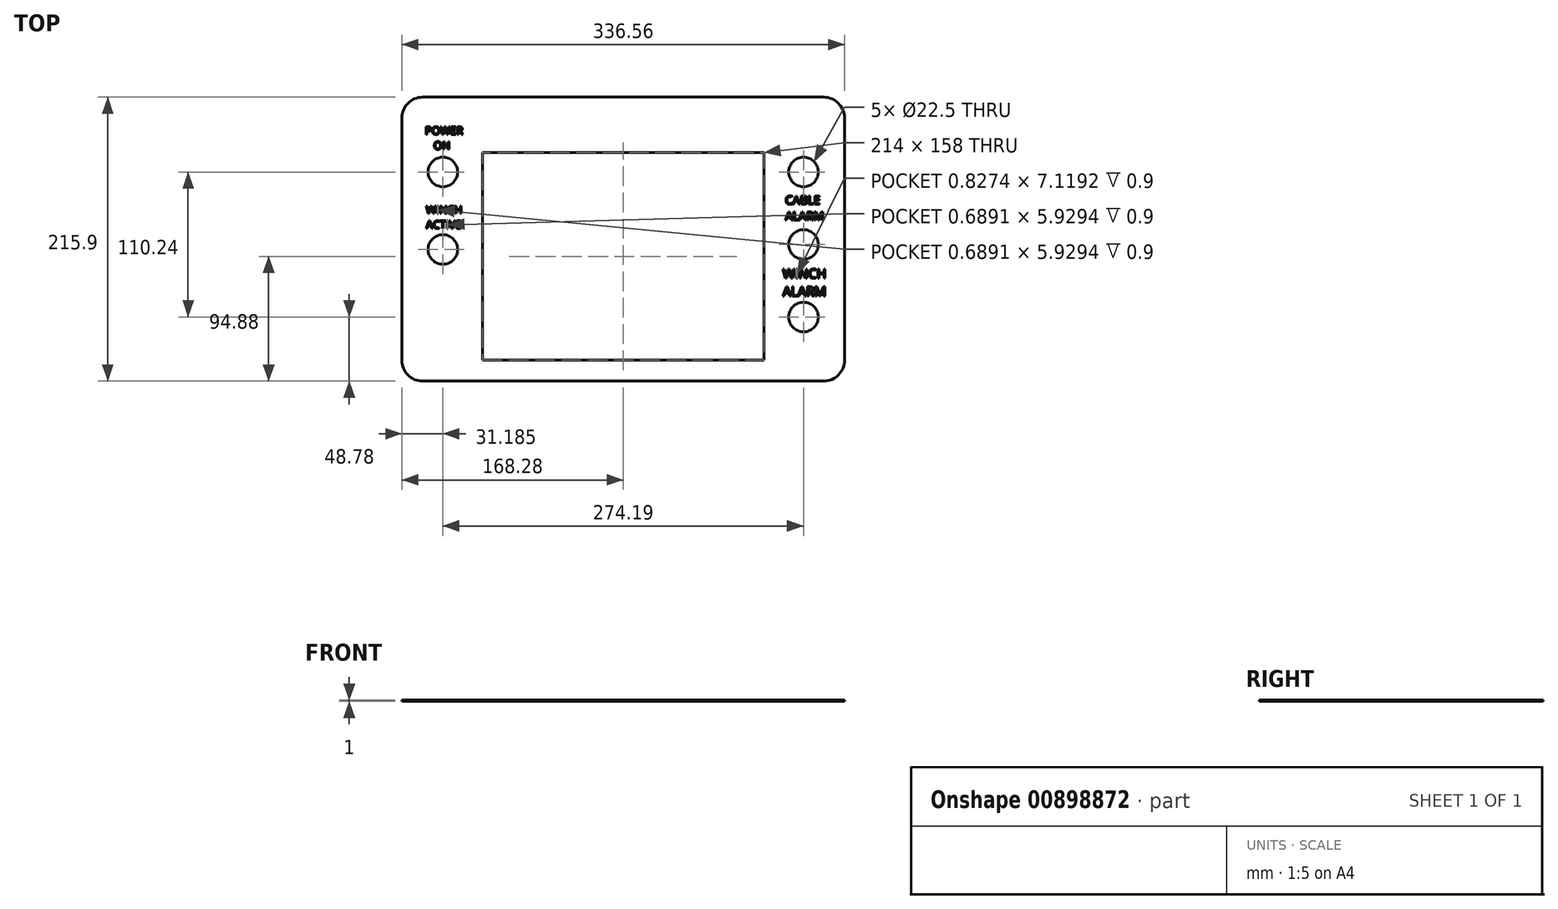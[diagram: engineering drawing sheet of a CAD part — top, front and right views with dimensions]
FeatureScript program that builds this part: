
annotation { "Feature Type Name" : "Feature", "Feature Type Description" : "" }
export const myFeature = defineFeature(function(context is Context, id is Id, definition is map)
    precondition{}
    {
        {
            var Q0;
            Q0=qCreatedBy(makeId("Top.planeOp"),FACE);
            var sketch = newSketch(context, id + "F0", { "sketchPlane" : qUnion([Q0])});
            skLineSegment(sketch, "E0.bottom", {"start": v(168.28, -107.95) * mm, "end": v(-168.28, -107.95) * mm});
            skLineSegment(sketch, "E0.top", {"start": v(168.28, 107.95) * mm, "end": v(-168.28, 107.95) * mm});
            skLineSegment(sketch, "E0.left", {"start": v(168.28, -107.95) * mm, "end": v(168.28, 107.95) * mm});
            skLineSegment(sketch, "E0.right", {"start": v(-168.28, -107.95) * mm, "end": v(-168.28, 107.95) * mm});
            skPoint(sketch, "E0.middle", {"position": v(0, 0) * mm});
            skCircle(sketch, "E1", {"center": v(-137.1, 51.07) * mm, "radius": 11.25 * mm});
            skCircle(sketch, "E2", {"center": v(-137.1, -7.85) * mm, "radius": 11.25 * mm});
            skCircle(sketch, "E3", {"center": v(137.1, 51.07) * mm, "radius": 11.25 * mm});
            skCircle(sketch, "E4", {"center": v(137.1, -4.05) * mm, "radius": 11.25 * mm});
            skCircle(sketch, "E5", {"center": v(137.1, -59.17) * mm, "radius": 11.25 * mm});
            skLineSegment(sketch, "E6.bottom", {"start": v(107, -92.07) * mm, "end": v(-107, -92.07) * mm});
            skLineSegment(sketch, "E6.top", {"start": v(107, 65.93) * mm, "end": v(-107, 65.93) * mm});
            skLineSegment(sketch, "E6.left", {"start": v(107, -92.07) * mm, "end": v(107, 65.93) * mm});
            skLineSegment(sketch, "E6.right", {"start": v(-107, -92.07) * mm, "end": v(-107, 65.93) * mm});
            skPoint(sketch, "E6.middle", {"position": v(0, -13.07) * mm});
            skSolve(sketch);
        }
        {
            var Q0;
            Q0 = qSketchRegion(id + "F0", true);
            extrude(context, id + "F1", {"entities" : qUnion([Q0]), "depth" : 1 * mm, "offsetDistance" : 25 * mm});
        }
        {
            var Q0;
            Q0=makeQuery(id+"F1.opExtrude","SWEPT_EDGE",EDGE,{"disambiguationData":[OSD([sQuery(id+"F0.wireOp",EDGE,"E0.bottom"),sQuery(id+"F0.wireOp",EDGE,"E0.right")])]});
            var Q1;
            Q1=makeQuery(id+"F1.opExtrude","SWEPT_EDGE",EDGE,{"disambiguationData":[OSD([sQuery(id+"F0.wireOp",EDGE,"E0.top"),sQuery(id+"F0.wireOp",EDGE,"E0.right")])]});
            var Q2;
            Q2=makeQuery(id+"F1.opExtrude","SWEPT_EDGE",EDGE,{"disambiguationData":[OSD([sQuery(id+"F0.wireOp",EDGE,"E0.top"),sQuery(id+"F0.wireOp",EDGE,"E0.left")])]});
            var Q3;
            Q3=makeQuery(id+"F1.opExtrude","SWEPT_EDGE",EDGE,{"disambiguationData":[OSD([sQuery(id+"F0.wireOp",EDGE,"E0.bottom"),sQuery(id+"F0.wireOp",EDGE,"E0.left")])]});
            fillet(context, id + "F2", {"entities" : qUnion([Q0, Q1, Q2, Q3]), "radius" : 15.88 * mm, "tangentPropagation" : true, "allowEdgeOverflow" : false});
        }
        {
            var Q0;
            Q0=makeQuery(id+"F1.opExtrude","CAP_FACE",FACE,{"disambiguationData":[OSD([sQuery(id+"F0.wireOp",EDGE,"E0.bottom"),sQuery(id+"F0.wireOp",EDGE,"E0.top"),sQuery(id+"F0.wireOp",EDGE,"E0.left"),sQuery(id+"F0.wireOp",EDGE,"E0.right"),sQuery(id+"F0.wireOp",EDGE,"E1"),sQuery(id+"F0.wireOp",EDGE,"E2"),sQuery(id+"F0.wireOp",EDGE,"E3"),sQuery(id+"F0.wireOp",EDGE,"E4"),sQuery(id+"F0.wireOp",EDGE,"E5"),sQuery(id+"F0.wireOp",EDGE,"E6.bottom"),sQuery(id+"F0.wireOp",EDGE,"E6.top"),sQuery(id+"F0.wireOp",EDGE,"E6.left"),sQuery(id+"F0.wireOp",EDGE,"E6.right")])],"isStart":false});
            var sketch = newSketch(context, id + "F3", { "sketchPlane" : qUnion([Q0])});
            skText(sketch, "E7", { "text": "POWER\n   ON", "fontName": "OpenSans-Regular.ttf"});
            skText(sketch, "E8", { "text": "WINCH\nACTIVE", "fontName": "OpenSans-Regular.ttf"});
            skText(sketch, "E9", { "text": "WINCH\nALARM", "fontName": "OpenSans-Regular.ttf"});
            skText(sketch, "E10", { "text": "CABLE\nALARM", "fontName": "OpenSans-Regular.ttf"});
            const initialGuessF3  = {"E7": [-0.15063, 0.07956, 1, 0, 0.00598], "E8": [-0.14988, 0.01936, 1, 0, 0.00598], "E9": [0.12128, -0.02975, 1, 0, 0.00718], "E10": [0.12318, 0.02655, 1, 0, 0.00642]};
            skSetInitialGuess(sketch, initialGuessF3);
            skSolve(sketch);
        }
        {
            var Q0;
            Q0 = qSketchRegion(id + "F3", true);
            extrude(context, id + "F4", {"entities" : qUnion([Q0]), "operationType" : NewBodyOperationType.REMOVE, "oppositeDirection" : true, "depth" : 0.9 * mm, "offsetDistance" : 25 * mm});
        }
    });
